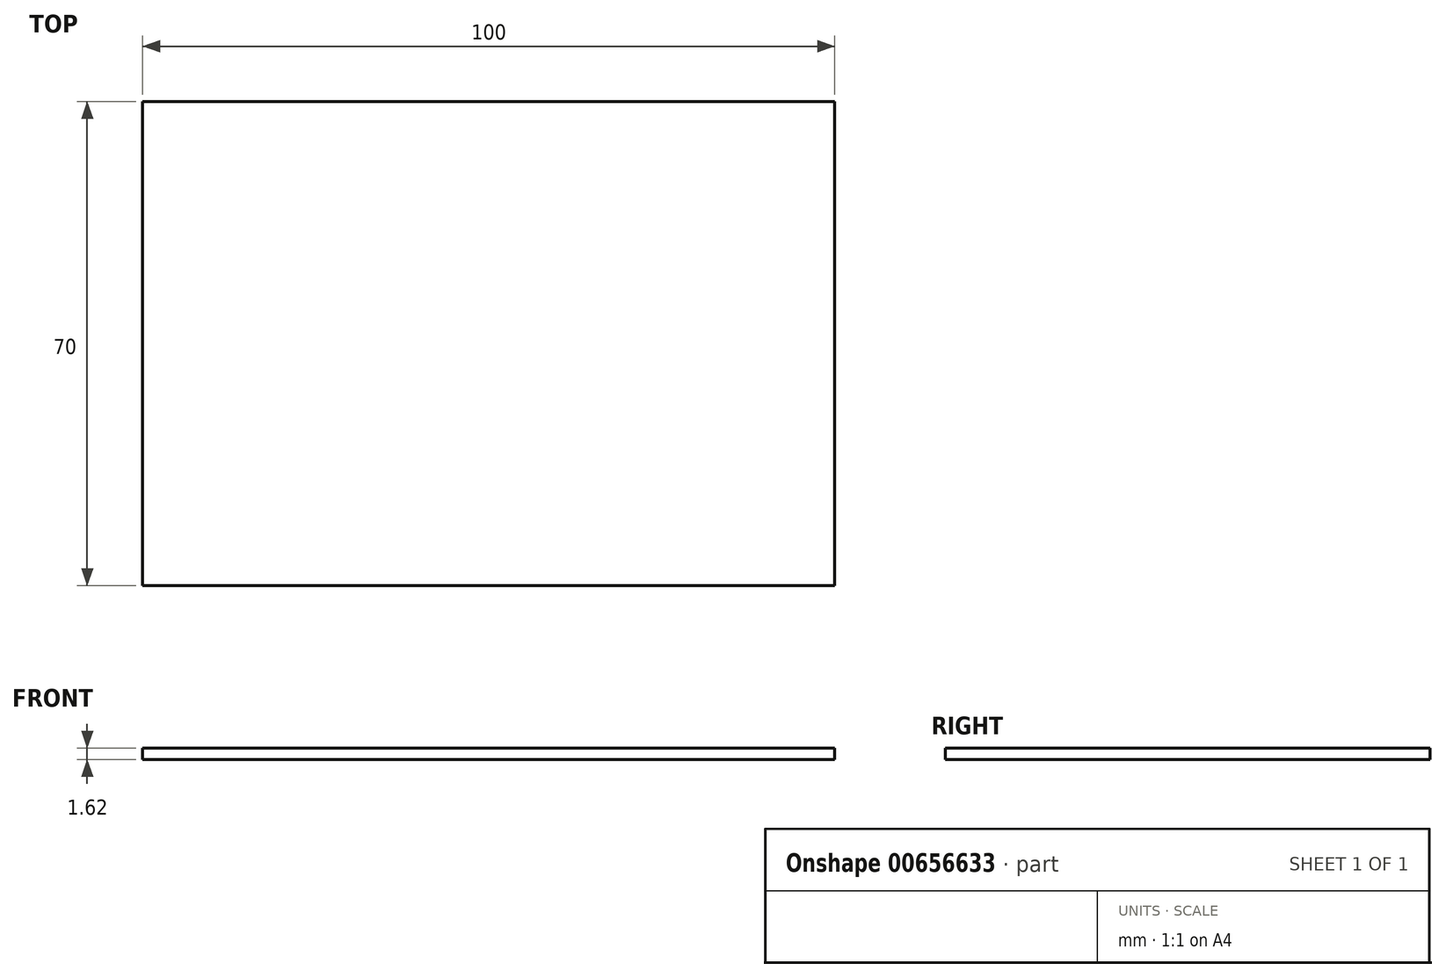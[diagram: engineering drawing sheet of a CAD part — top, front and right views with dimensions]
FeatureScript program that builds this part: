
annotation { "Feature Type Name" : "Feature", "Feature Type Description" : "" }
export const myFeature = defineFeature(function(context is Context, id is Id, definition is map)
    precondition{}
    {
        {
            var Q0;
            Q0=qCreatedBy(makeId("Top.planeOp"),FACE);
            var sketch = newSketch(context, id + "F0", { "sketchPlane" : qUnion([Q0])});
            skLineSegment(sketch, "E0.bottom", {"start": v(-0.08, 0.05) * mm, "end": v(99.92, 0.05) * mm});
            skLineSegment(sketch, "E0.top", {"start": v(-0.08, 70.05) * mm, "end": v(99.92, 70.05) * mm});
            skLineSegment(sketch, "E0.left", {"start": v(-0.08, 0.05) * mm, "end": v(-0.08, 70.05) * mm});
            skLineSegment(sketch, "E0.right", {"start": v(99.92, 0.05) * mm, "end": v(99.92, 70.05) * mm});
            skSolve(sketch);
        }
        {
            var Q0;
            Q0=makeQuery(id+"F0.imprint","IMPRINT",FACE,{"disambiguationData":[TD([[makeQuery(id+"F0.imprint","IMPRINT",EDGE,{"derivedFrom":sQuery(id+"F0.wireOp",EDGE,"E0.bottom")}),1.0]])]});
            extrude(context, id + "F1", {"entities" : qUnion([Q0]), "depth" : 1.62 * mm, "offsetDistance" : 25 * mm});
        }
    });
